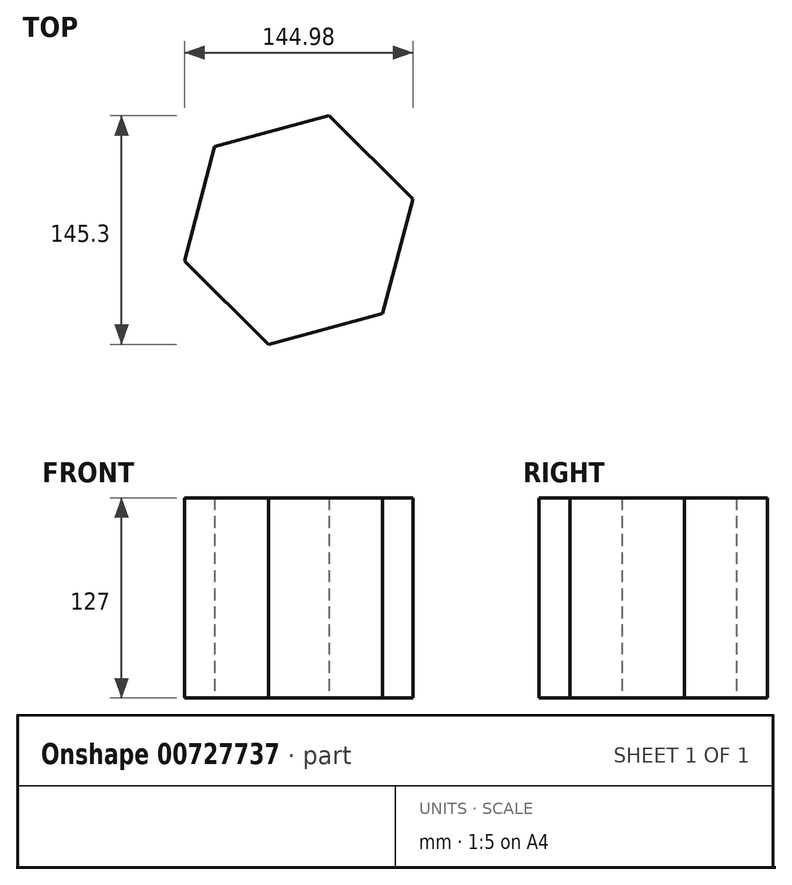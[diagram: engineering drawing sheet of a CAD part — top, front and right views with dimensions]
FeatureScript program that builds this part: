
annotation { "Feature Type Name" : "Feature", "Feature Type Description" : "" }
export const myFeature = defineFeature(function(context is Context, id is Id, definition is map)
    precondition{}
    {
        {
            var Q0;
            Q0=qCreatedBy(makeId("Top.planeOp"),FACE);
            var sketch = newSketch(context, id + "F0", { "sketchPlane" : qUnion([Q0])});
            skCircle(sketch, "E0.cCircle", {"center": v(-55.1, -7.1) * mm, "radius": 65.06 * mm, "construction": true});
            skLineSegment(sketch, "E0.0", {"start": v(17.39, 12.65) * mm, "end": v(-1.76, -60) * mm});
            skLineSegment(sketch, "E0.1", {"start": v(-1.76, -60) * mm, "end": v(-74.25, -79.74) * mm});
            skLineSegment(sketch, "E0.2", {"start": v(-74.25, -79.74) * mm, "end": v(-127.6, -26.83) * mm});
            skLineSegment(sketch, "E0.3", {"start": v(-127.6, -26.83) * mm, "end": v(-108.44, 45.81) * mm});
            skLineSegment(sketch, "E0.4", {"start": v(-108.44, 45.81) * mm, "end": v(-35.95, 65.56) * mm});
            skLineSegment(sketch, "E0.5", {"start": v(-35.95, 65.56) * mm, "end": v(17.39, 12.65) * mm});
            skPoint(sketch, "E0.0.midPoint", {"position": v(7.82, -23.68) * mm});
            skSolve(sketch);
        }
        {
            var Q0;
            Q0=makeQuery(id+"F0.imprint","IMPRINT",FACE,{"disambiguationData":[TD([[makeQuery(id+"F0.imprint","IMPRINT",EDGE,{"derivedFrom":sQuery(id+"F0.wireOp",EDGE,"E0.0")}),-1.0]])]});
            extrude(context, id + "F1", {"entities" : qUnion([Q0]), "depth" : 127 * mm, "offsetDistance" : 25.4 * mm});
        }
    });
